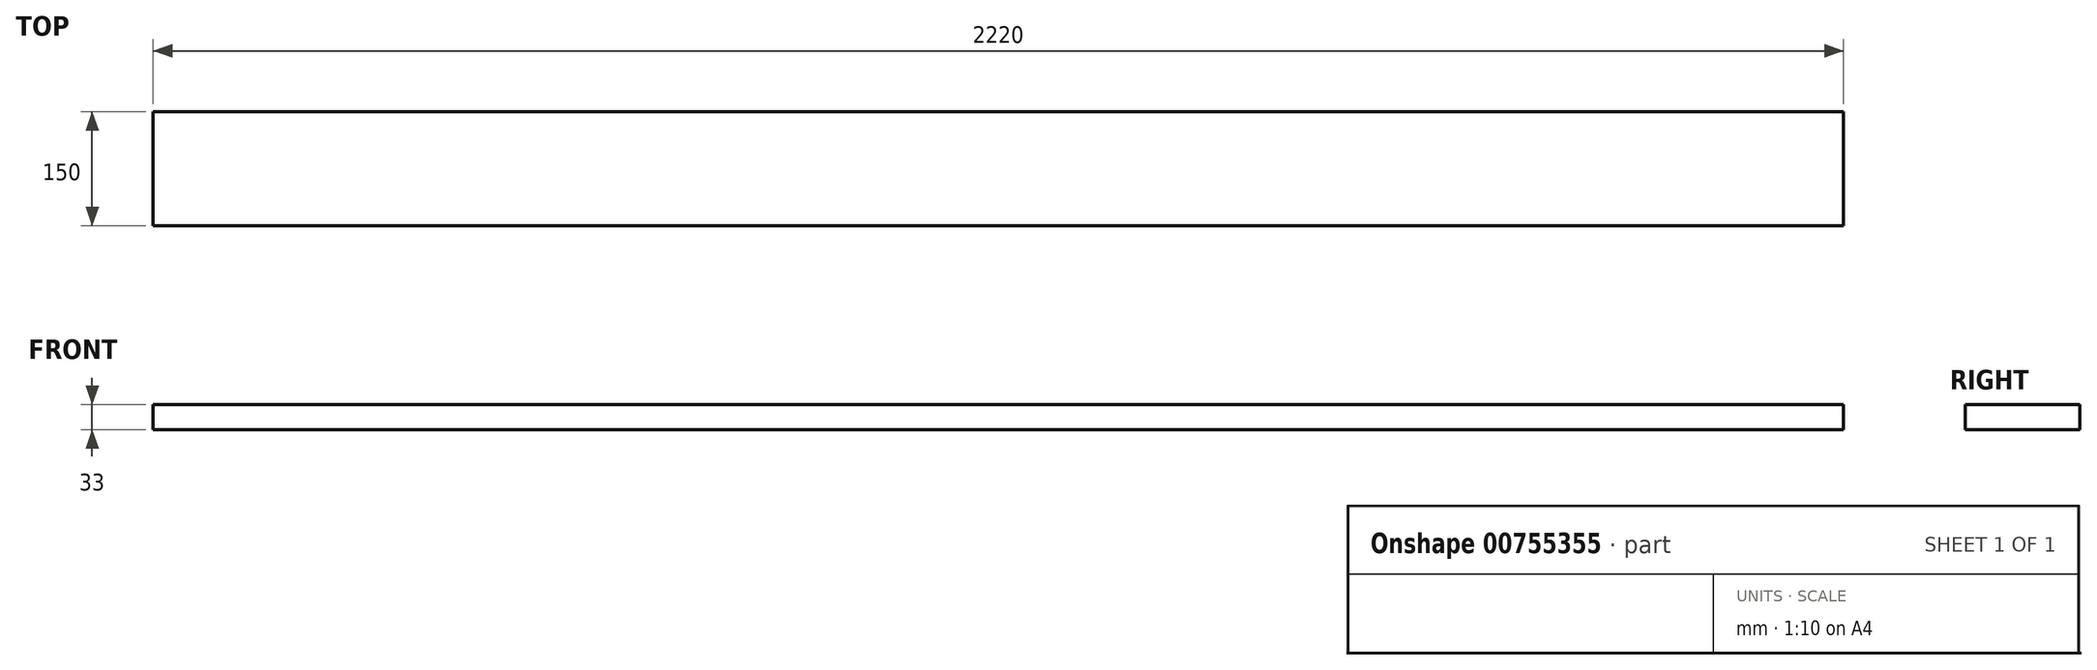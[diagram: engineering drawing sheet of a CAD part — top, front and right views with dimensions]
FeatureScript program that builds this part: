
annotation { "Feature Type Name" : "Feature", "Feature Type Description" : "" }
export const myFeature = defineFeature(function(context is Context, id is Id, definition is map)
    precondition{}
    {
        {
            var Q0;
            Q0=qCreatedBy(makeId("Right.planeOp"),FACE);
            var sketch = newSketch(context, id + "F0", { "sketchPlane" : qUnion([Q0])});
            skLineSegment(sketch, "E0.bottom", {"start": v(75, 16.5) * mm, "end": v(-75, 16.5) * mm});
            skLineSegment(sketch, "E0.top", {"start": v(75, -16.5) * mm, "end": v(-75, -16.5) * mm});
            skLineSegment(sketch, "E0.left", {"start": v(75, 16.5) * mm, "end": v(75, -16.5) * mm});
            skLineSegment(sketch, "E0.right", {"start": v(-75, 16.5) * mm, "end": v(-75, -16.5) * mm});
            skPoint(sketch, "E0.middle", {"position": v(0, 0) * mm});
            skSolve(sketch);
        }
        {
            var Q0;
            Q0=qSketchRegion(id+"F0",true);
            extrude(context, id + "F1", {"entities" : qUnion([Q0]), "endBound" : BoundingType.SYMMETRIC, "depth" : 2220 * mm, "offsetDistance" : 25 * mm});
        }
    });
